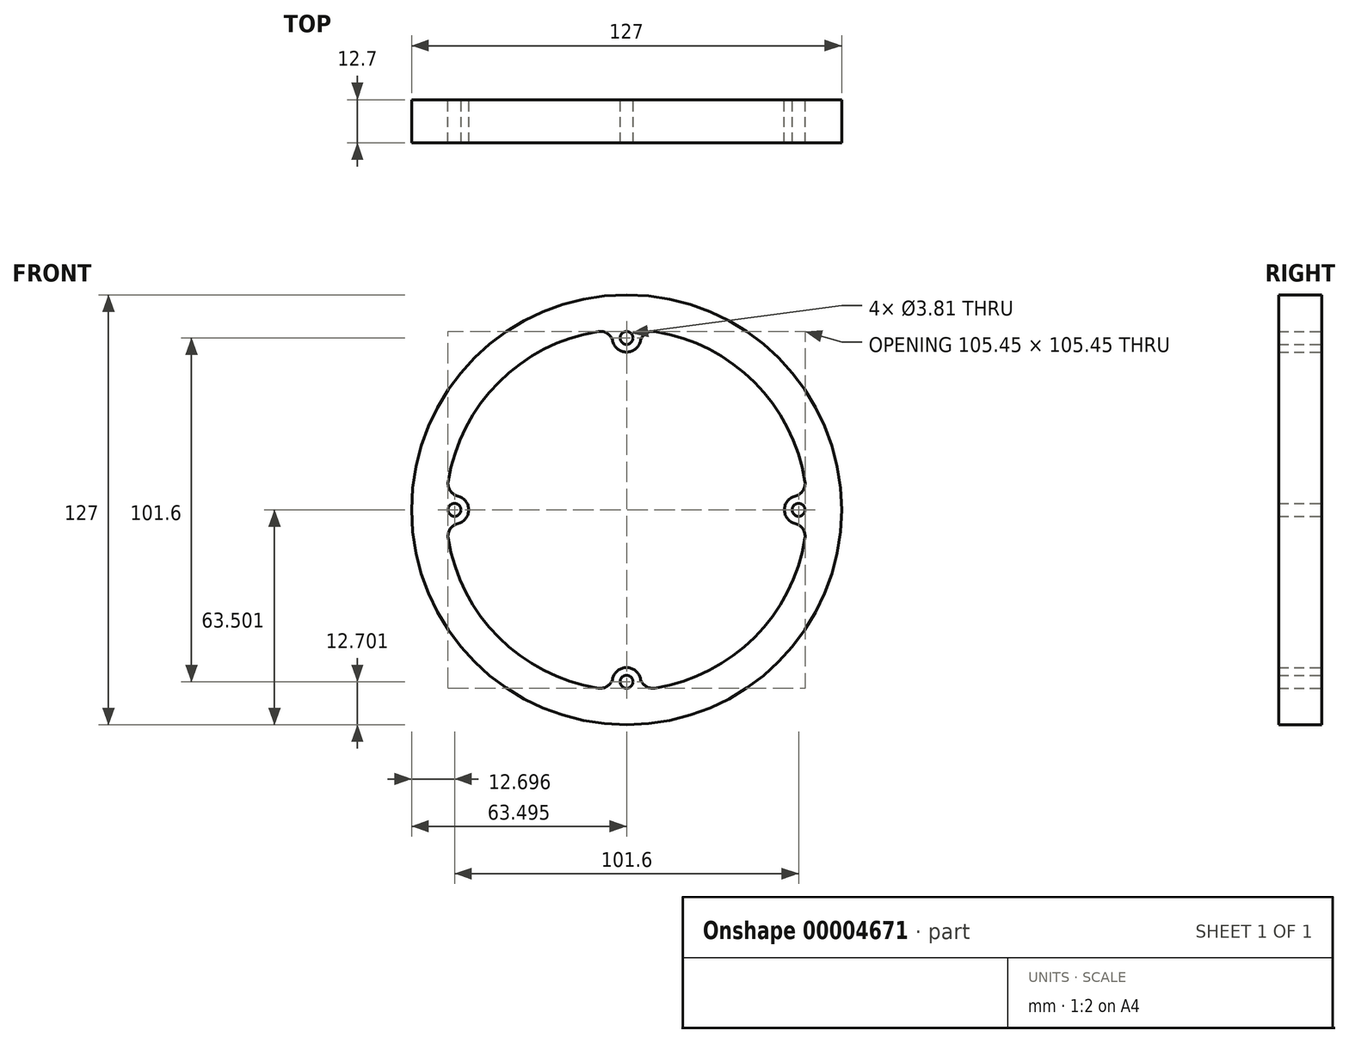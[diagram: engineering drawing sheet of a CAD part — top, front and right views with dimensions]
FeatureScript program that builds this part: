
annotation { "Feature Type Name" : "Feature", "Feature Type Description" : "" }
export const myFeature = defineFeature(function(context is Context, id is Id, definition is map)
    precondition{}
    {
        {
            var Q0;
            Q0=qCreatedBy(makeId("Front.planeOp"),FACE);
            var sketch = newSketch(context, id + "F0", { "sketchPlane" : qUnion([Q0])});
            skCircle(sketch, "E0", {"center": v(-7.58, 9.9) * mm, "radius": 63.5 * mm});
            skArc(sketch, "E1", {"start": v(22.52, 53.92) * mm, "mid": v(12.13, 59.45) * mm, "end": v(0.79, 62.57) * mm});
            skLineSegment(sketch, "E2", {"start": v(-7.58, 73.4) * mm, "end": v(-7.58, -53.6) * mm, "construction": true});
            skLineSegment(sketch, "E3", {"start": v(-71.08, 9.9) * mm, "end": v(55.92, 9.9) * mm, "construction": true});
            skCircle(sketch, "E4", {"center": v(-7.58, 9.9) * mm, "radius": 50.8 * mm, "construction": true});
            skCircle(sketch, "E5", {"center": v(-7.58, 60.7) * mm, "radius": 1.9 * mm});
            skCircle(sketch, "E6", {"center": v(-7.58, -40.9) * mm, "radius": 1.9 * mm});
            skCircle(sketch, "E7", {"center": v(43.22, 9.9) * mm, "radius": 1.9 * mm});
            skCircle(sketch, "E8", {"center": v(-58.38, 9.9) * mm, "radius": 1.9 * mm});
            skArc(sketch, "E9", {"start": v(42.23, 13.96) * mm, "mid": v(39.02, 9.9) * mm, "end": v(42.23, 5.82) * mm});
            skArc(sketch, "E10", {"start": v(-3.51, -39.92) * mm, "mid": v(-7.58, -36.72) * mm, "end": v(-11.66, -39.92) * mm});
            skArc(sketch, "E11.trimOffspring", {"start": v(0.79, -42.79) * mm, "mid": v(30.13, -27.83) * mm, "end": v(45.1, 1.52) * mm});
            skArc(sketch, "E12", {"start": v(-57.4, 5.82) * mm, "mid": v(-54.2, 9.9) * mm, "end": v(-57.4, 13.96) * mm});
            skArc(sketch, "E13", {"start": v(-11.66, 59.7) * mm, "mid": v(-7.58, 56.5) * mm, "end": v(-3.51, 59.7) * mm});
            skArc(sketch, "E14.trimOffspring", {"start": v(-50.71, 41.28) * mm, "mid": v(-56.85, 30.34) * mm, "end": v(-60.26, 18.27) * mm});
            skArc(sketch, "E15.trimOffspring", {"start": v(-60.26, 1.52) * mm, "mid": v(-56.6, -11.14) * mm, "end": v(-49.95, -22.52) * mm});
            skPoint(sketch, "E16.visualSharp", {"position": v(-60.82, 6.48) * mm});
            skArc(sketch, "E16.filletArc", {"start": v(-57.4, 5.82) * mm, "mid": v(-59.67, 4.23) * mm, "end": v(-60.26, 1.52) * mm});
            skPoint(sketch, "E17.visualSharp", {"position": v(-60.82, 13.3) * mm});
            skArc(sketch, "E17.filletArc", {"start": v(-60.26, 18.27) * mm, "mid": v(-59.67, 15.55) * mm, "end": v(-57.4, 13.96) * mm});
            skPoint(sketch, "E18.visualSharp", {"position": v(-47.59, 45.17) * mm});
            skPoint(sketch, "E19.visualSharp", {"position": v(-46.74, -26.33) * mm});
            skPoint(sketch, "E20.visualSharp", {"position": v(-41.79, -31.04) * mm});
            skPoint(sketch, "E21.visualSharp", {"position": v(-4.17, -43.34) * mm});
            skArc(sketch, "E21.filletArc", {"start": v(-3.51, -39.92) * mm, "mid": v(-1.92, -42.2) * mm, "end": v(0.79, -42.79) * mm});
            skPoint(sketch, "E22.visualSharp", {"position": v(-11, -43.34) * mm});
            skArc(sketch, "E22.filletArc", {"start": v(-15.96, -42.79) * mm, "mid": v(-13.25, -42.2) * mm, "end": v(-11.66, -39.92) * mm});
            skPoint(sketch, "E23.visualSharp", {"position": v(-42.75, 50) * mm});
            skArc(sketch, "E24.trimOffspring", {"start": v(-15.96, 62.57) * mm, "mid": v(-27.96, 59.19) * mm, "end": v(-38.85, 53.1) * mm});
            skPoint(sketch, "E25.visualSharp", {"position": v(-11, 63.12) * mm});
            skArc(sketch, "E25.filletArc", {"start": v(-11.66, 59.7) * mm, "mid": v(-13.25, 61.98) * mm, "end": v(-15.96, 62.57) * mm});
            skPoint(sketch, "E26.visualSharp", {"position": v(-4.17, 63.12) * mm});
            skArc(sketch, "E26.filletArc", {"start": v(0.79, 62.57) * mm, "mid": v(-1.92, 61.98) * mm, "end": v(-3.51, 59.7) * mm});
            skPoint(sketch, "E27.visualSharp", {"position": v(26.5, 50.92) * mm});
            skPoint(sketch, "E28.visualSharp", {"position": v(31.47, 46.23) * mm});
            skArc(sketch, "E29.trimOffspring", {"start": v(45.1, 18.27) * mm, "mid": v(41.4, 31) * mm, "end": v(34.7, 42.42) * mm});
            skPoint(sketch, "E30.visualSharp", {"position": v(45.65, 6.48) * mm});
            skArc(sketch, "E30.filletArc", {"start": v(45.1, 1.52) * mm, "mid": v(44.5, 4.23) * mm, "end": v(42.23, 5.82) * mm});
            skPoint(sketch, "E31.visualSharp", {"position": v(45.65, 13.3) * mm});
            skArc(sketch, "E31.filletArc", {"start": v(42.23, 13.96) * mm, "mid": v(44.5, 15.55) * mm, "end": v(45.1, 18.27) * mm});
            skArc(sketch, "E32.trimOffspring", {"start": v(35.75, -21.2) * mm, "mid": v(41.75, -10.4) * mm, "end": v(45.1, 1.52) * mm});
            skPoint(sketch, "E33.visualSharp", {"position": v(32.68, -25.1) * mm});
            skPoint(sketch, "E34.visualSharp", {"position": v(27.51, -30.28) * mm});
            skArc(sketch, "E35.trimOffspring", {"start": v(-60.26, 1.52) * mm, "mid": v(-45.3, -27.83) * mm, "end": v(-15.96, -42.79) * mm});
            skArc(sketch, "E36.trimOffspring", {"start": v(-15.96, 62.57) * mm, "mid": v(-45.3, 47.6) * mm, "end": v(-60.26, 18.27) * mm});
            skArc(sketch, "E37.trimOffspring", {"start": v(45.1, 18.27) * mm, "mid": v(30.13, 47.6) * mm, "end": v(0.79, 62.57) * mm});
            skSolve(sketch);
        }
        {
            var Q0;
            Q0=makeQuery(id+"F0.imprint","IMPRINT",FACE,{"disambiguationData":[TD([[makeQuery(id+"F0.imprint","IMPRINT",EDGE,{"derivedFrom":sQuery(id+"F0.wireOp",EDGE,"E0")}),1.0]])]});
            extrude(context, id + "F1", {"entities" : qUnion([Q0]), "depth" : 12.7 * mm});
        }
    });
